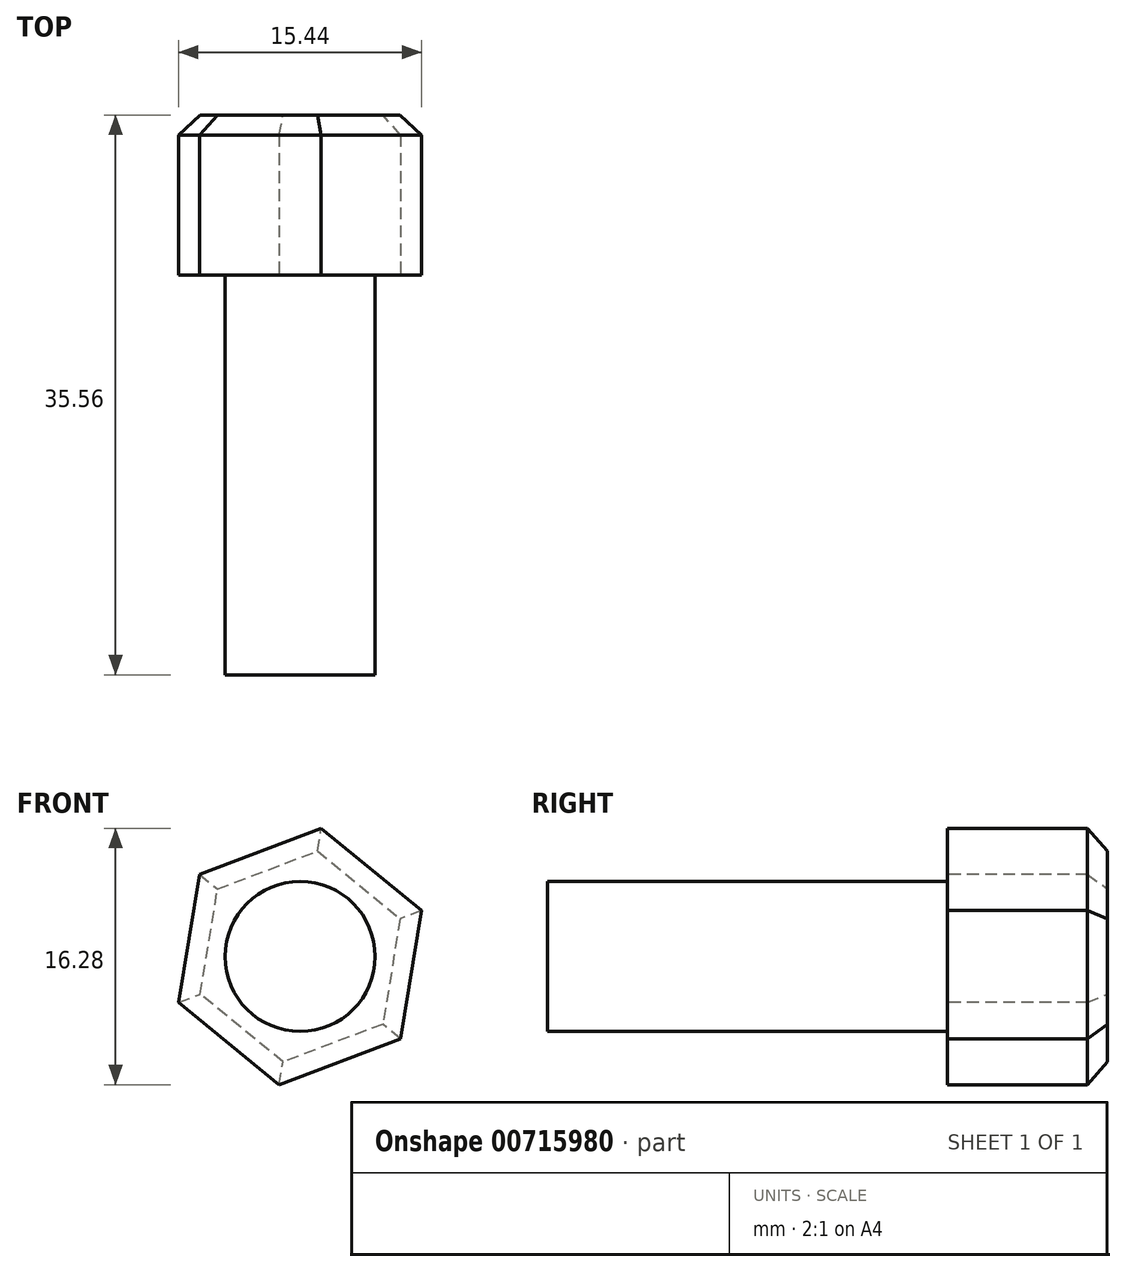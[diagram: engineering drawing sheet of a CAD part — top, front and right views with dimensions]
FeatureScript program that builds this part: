
annotation { "Feature Type Name" : "Feature", "Feature Type Description" : "" }
export const myFeature = defineFeature(function(context is Context, id is Id, definition is map)
    precondition{}
    {
        {
            var Q0;
            Q0=qCreatedBy(makeId("Front.planeOp"),FACE);
            var sketch = newSketch(context, id + "F0", { "sketchPlane" : qUnion([Q0])});
            skCircle(sketch, "E0.cCircle", {"center": v(0, 0) * mm, "radius": 7.14 * mm, "construction": true});
            skLineSegment(sketch, "E0.0", {"start": v(1.33, 8.14) * mm, "end": v(7.72, 2.92) * mm});
            skLineSegment(sketch, "E0.1", {"start": v(7.72, 2.92) * mm, "end": v(6.38, -5.22) * mm});
            skLineSegment(sketch, "E0.2", {"start": v(6.38, -5.22) * mm, "end": v(-1.33, -8.14) * mm});
            skLineSegment(sketch, "E0.3", {"start": v(-1.33, -8.14) * mm, "end": v(-7.72, -2.92) * mm});
            skLineSegment(sketch, "E0.4", {"start": v(-7.72, -2.92) * mm, "end": v(-6.38, 5.22) * mm});
            skLineSegment(sketch, "E0.5", {"start": v(-6.38, 5.22) * mm, "end": v(1.33, 8.14) * mm});
            skPoint(sketch, "E0.0.midPoint", {"position": v(4.52, 5.53) * mm});
            skSolve(sketch);
        }
        {
            var Q0;
            Q0 = qSketchRegion(id + "F0", true);
            extrude(context, id + "F1", {"entities" : qUnion([Q0]), "oppositeDirection" : true, "depth" : 10.16 * mm, "offsetDistance" : 25.4 * mm});
        }
        {
            var Q0;
            Q0=qCreatedBy(makeId("Front.planeOp"),FACE);
            var sketch = newSketch(context, id + "F2", { "sketchPlane" : qUnion([Q0])});
            skCircle(sketch, "E1", {"center": v(0, 0) * mm, "radius": 4.76 * mm});
            skSolve(sketch);
        }
        {
            var Q0;
            Q0 = qSketchRegion(id + "F2", true);
            extrude(context, id + "F3", {"entities" : qUnion([Q0]), "operationType" : NewBodyOperationType.ADD, "depth" : 25.4 * mm, "offsetDistance" : 25.4 * mm});
        }
        {
            var Q0;
            Q0=makeQuery(id+"F1.opExtrude","CAP_EDGE",EDGE,{"disambiguationData":[OSD([sQuery(id+"F0.wireOp",EDGE,"E0.4")])],"isStart":false});
            var Q1;
            Q1=makeQuery(id+"F1.opExtrude","CAP_EDGE",EDGE,{"disambiguationData":[OSD([sQuery(id+"F0.wireOp",EDGE,"E0.5")])],"isStart":false});
            var Q2;
            Q2=makeQuery(id+"F1.opExtrude","CAP_EDGE",EDGE,{"disambiguationData":[OSD([sQuery(id+"F0.wireOp",EDGE,"E0.0")])],"isStart":false});
            var Q3;
            Q3=makeQuery(id+"F1.opExtrude","CAP_EDGE",EDGE,{"disambiguationData":[OSD([sQuery(id+"F0.wireOp",EDGE,"E0.3")])],"isStart":false});
            var Q4;
            Q4=makeQuery(id+"F1.opExtrude","CAP_EDGE",EDGE,{"disambiguationData":[OSD([sQuery(id+"F0.wireOp",EDGE,"E0.2")])],"isStart":false});
            var Q5;
            Q5=makeQuery(id+"F1.opExtrude","CAP_EDGE",EDGE,{"disambiguationData":[OSD([sQuery(id+"F0.wireOp",EDGE,"E0.1")])],"isStart":false});
            chamfer(context, id + "F4", {"entities" : qUnion([Q0, Q1, Q2, Q3, Q4, Q5]), "width" : 1.27 * mm, "tangentPropagation" : true});
        }
    });
